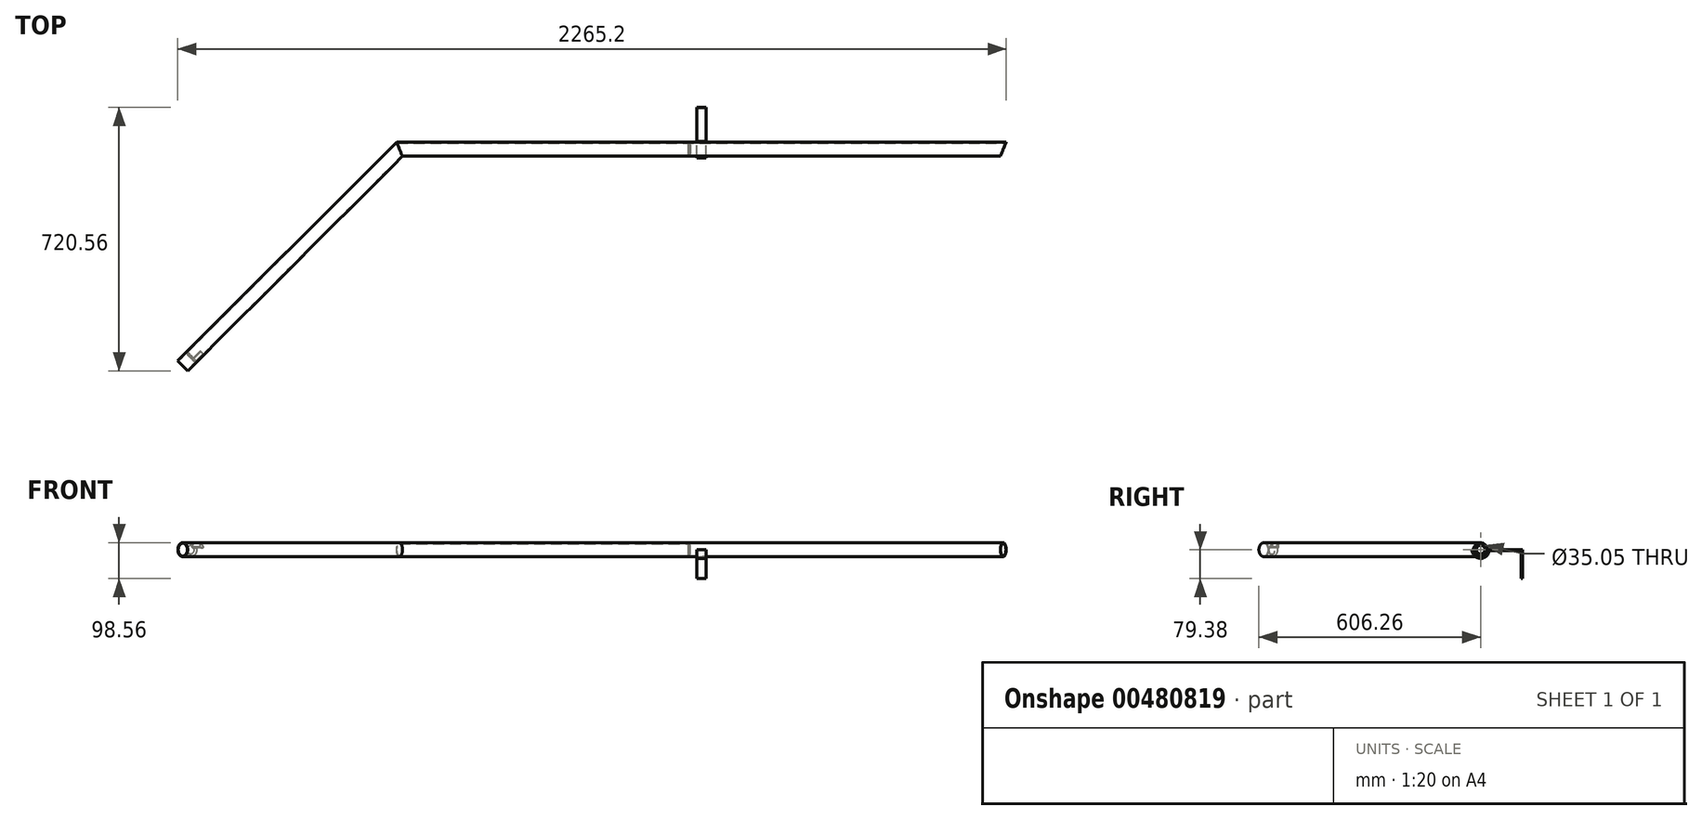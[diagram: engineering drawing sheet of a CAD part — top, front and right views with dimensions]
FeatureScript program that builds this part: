
annotation { "Feature Type Name" : "Feature", "Feature Type Description" : "" }
export const myFeature = defineFeature(function(context is Context, id is Id, definition is map)
    precondition{}
    {
        {
            assignVariable(context, id + "F0", {"name" : "sidelength", "anyValue" : 33});
        }
        {
            assignVariable(context, id + "F1", {"name" : "centerlength", "anyValue" : 65});
        }
        {
            var Q0;
            Q0=qCreatedBy(makeId("Top.planeOp"),FACE);
            var sketch = newSketch(context, id + "F2", { "sketchPlane" : qUnion([Q0])});
            skLineSegment(sketch, "E0", {"start": v(876.3, 114.3) * mm, "end": v(-876.3, 114.3) * mm});
            skLineSegment(sketch, "E1", {"start": v(-876.3, 114.3) * mm, "end": v(-1482.72, -500.56) * mm});
            skLineSegment(sketch, "E2", {"start": v(876.3, 114.3) * mm, "end": v(1482.73, -500.56) * mm});
            skLineSegment(sketch, "E3", {"start": v(-1482.72, -500.56) * mm, "end": v(1482.73, -500.56) * mm});
            skSolve(sketch);
        }
        {
            var Q0;
            Q0=qCreatedBy(makeId("Top.planeOp"),FACE);
            var sketch = newSketch(context, id + "F3", { "sketchPlane" : qUnion([Q0])});
            skLineSegment(sketch, "E4", {"start": v(-1418.2, -592.7) * mm, "end": v(-825.5, 0) * mm});
            skLineSegment(sketch, "E5", {"start": v(-825.5, 0) * mm, "end": v(825.5, 0) * mm});
            skLineSegment(sketch, "E6", {"start": v(825.5, 0) * mm, "end": v(1418.2, -592.7) * mm});
            skLineSegment(sketch, "E7", {"start": v(-825.5, 0) * mm, "end": v(-822.64, -6.9) * mm});
            skSolve(sketch);
        }
        {
            var Q0;
            Q0=sQuery(id+"F3.wireOp",VERTEX,"E4.start");
            var Q1;
            Q1=sQuery(id+"F3.wireOp",EDGE,"E4");
            cPlane(context, id + "F4", {"entities" : qUnion([Q0, Q1]), "cplaneType" : CPlaneType.LINE_POINT, "offset" : 25.4 * mm, "width" : 152.4 * mm, "height" : 152.4 * mm});
        }
        {
            var Q0;
            Q0=sQuery(id+"F3.wireOp",EDGE,"E7");
            cPlane(context, id + "F5", {"entities" : qUnion([Q0]), "cplaneType" : CPlaneType.LINE_ANGLE, "offset" : 25.4 * mm, "angle" : 90 * degree, "width" : 152.4 * mm, "height" : 152.4 * mm});
        }
        {
            var Q0;
            Q0=qCreatedBy(id+"F4.planeOp",FACE);
            var sketch = newSketch(context, id + "F6", { "sketchPlane" : qUnion([Q0])});
            skCircle(sketch, "E8", {"center": v(583.72, 0) * mm, "radius": 19.18 * mm});
            skCircle(sketch, "E9", {"center": v(583.72, 0) * mm, "radius": 17.53 * mm});
            skSolve(sketch);
        }
        {
            var Q0;
            Q0 = qSketchRegion(id + "F6", true);
            var Q1;
            Q1=qCreatedBy(id+"F5.planeOp",FACE);
            extrude(context, id + "F7", {"entities" : qUnion([Q0]), "endBound" : BoundingType.UP_TO_SURFACE, "endBoundEntityFace" : qUnion([Q1]), "depth" : ((getVariable(context, 'sidelength')) + (.1 * getVariable(context, 'sidelength'))) * mm});
        }
        {
            var Q0;
            Q0=qCreatedBy(id+"F4.planeOp",FACE);
            cPlane(context, id + "F8", {"entities" : qUnion([Q0]), "cplaneType" : CPlaneType.OFFSET, "offset" : (getVariable(context, 'sidelength') - 2) * mm, "width" : 152.4 * mm, "height" : 152.4 * mm});
        }
        {
            var Q0;
            Q0=qCreatedBy(id+"F8.planeOp",FACE);
            var sketch = newSketch(context, id + "F9", { "sketchPlane" : qUnion([Q0])});
            skCircle(sketch, "E10", {"center": v(583.72, 0) * mm, "radius": 17.4 * mm});
            skSolve(sketch);
        }
        {
            var Q0;
            Q0 = qSketchRegion(id + "F9", true);
            var Q1;
            Q1=qCreatedBy(id+"F5.planeOp",FACE);
            extrude(context, id + "F10", {"entities" : qUnion([Q0]), "endBound" : BoundingType.UP_TO_SURFACE, "endBoundEntityFace" : qUnion([Q1]), "depth" : 25.4 * mm});
        }
        {
            var Q0;
            Q0=qCreatedBy(makeId("Right.planeOp"),FACE);
            cPlane(context, id + "F11", {"entities" : qUnion([Q0]), "cplaneType" : CPlaneType.OFFSET, "offset" : (getVariable(context, 'centerlength') / 2 - 2) * mm, "oppositeDirection" : true, "width" : 152.4 * mm, "height" : 152.4 * mm});
        }
        {
            var Q0;
            Q0=qCreatedBy(id+"F11.planeOp",FACE);
            var sketch = newSketch(context, id + "F12", { "sketchPlane" : qUnion([Q0])});
            skCircle(sketch, "E11", {"center": v(0, 0) * mm, "radius": 16.9 * mm});
            skSolve(sketch);
        }
        {
            var Q0;
            Q0=makeQuery(id+"F12.imprint","IMPRINT",FACE,{"disambiguationData":[TD([[makeQuery(id+"F12.imprint","IMPRINT",EDGE,{"derivedFrom":sQuery(id+"F12.wireOp",EDGE,"E11")}),1.0]])]});
            var Q1;
            Q1=makeQuery(id+"F10.opExtrude","CAP_FACE",FACE,{"disambiguationData":[OSD([sQuery(id+"F9.wireOp",EDGE,"E10")])],"isStart":false});
            extrude(context, id + "F13", {"entities" : qUnion([Q0]), "operationType" : NewBodyOperationType.ADD, "endBound" : BoundingType.UP_TO_SURFACE, "oppositeDirection" : true, "endBoundEntityFace" : qUnion([Q1]), "depth" : 25.4 * mm});
        }
        {
            var Q0;
            Q0=makeQuery(id+"F10.opExtrude","CAP_FACE",FACE,{"disambiguationData":[OSD([sQuery(id+"F9.wireOp",EDGE,"E10")])],"isStart":true});
            var sketch = newSketch(context, id + "F14", { "sketchPlane" : qUnion([Q0])});
            skCircle(sketch, "E12", {"center": v(-583.72, 0) * mm, "radius": 8.9 * mm, "construction": true});
            skLineSegment(sketch, "E13", {"start": v(-583.72, 0) * mm, "end": v(-583.72, 17.4) * mm, "construction": true});
            skLineSegment(sketch, "E14", {"start": v(-583.72, 0) * mm, "end": v(-566.32, 0) * mm, "construction": true});
            skLineSegment(sketch, "E15", {"start": v(-576.42, 5.08) * mm, "end": v(-567.08, 5.08) * mm});
            skArc(sketch, "E16", {"start": v(-578.64, 7.3) * mm, "mid": v(-577.43, 6.29) * mm, "end": v(-576.42, 5.08) * mm});
            skLineSegment(sketch, "E17", {"start": v(-578.64, 7.3) * mm, "end": v(-578.64, 16.64) * mm});
            skArc(sketch, "E18", {"start": v(-578.64, 16.64) * mm, "mid": v(-571.41, 12.3) * mm, "end": v(-567.08, 5.08) * mm});
            skSolve(sketch);
        }
        {
            var Q0;
            Q0 = qSketchRegion(id + "F14", true);
            extrude(context, id + "F15", {"entities" : qUnion([Q0]), "operationType" : NewBodyOperationType.REMOVE, "oppositeDirection" : true, "depth" : 31.75 * mm, "offsetDistance" : 25.4 * mm});
        }
        {
            var Q0;
            {var subQ0=sQuery(id+"F9.wireOp",EDGE,"E10");var subQ4=makeQuery(id+"F15.boolean.opBoolean","COPY",FACE,{"derivedFrom":makeQuery(id+"F15.opExtrude","SWEPT_FACE",FACE,{"disambiguationData":[OSD([sQuery(id+"F14.wireOp",EDGE,"NrfxDNrx-Ji7I-Meca-oNIs-p1KaCWfqXKCt")])]})});Q0=makeQuery(id+"FA1yCE69HmIhhTY_2.3.F15.boolean.opBoolean","SPLIT",EDGE,{"disambiguationData":[TD([subQ4])],"derivedFrom":makeQuery(id+"FA1yCE69HmIhhTY_2.2.F15.boolean.opBoolean","SPLIT",EDGE,{"disambiguationData":[TD([subQ4])],"derivedFrom":makeQuery(id+"FA1yCE69HmIhhTY_2.1.F15.boolean.opBoolean","SPLIT",EDGE,{"disambiguationData":[TD([subQ4])],"derivedFrom":makeQuery(id+"F10.opExtrude","CAP_EDGE",EDGE,{"disambiguationData":[OSD([subQ0])],"isStart":true})})})});}
            var Q1;
            {var subQ0=sQuery(id+"F9.wireOp",EDGE,"E10");Q1=makeQuery(id+"FA1yCE69HmIhhTY_2.1.F15.boolean.opBoolean","SPLIT",EDGE,{"disambiguationData":[TD([makeQuery(id+"F15.boolean.opBoolean","COPY",FACE,{"derivedFrom":makeQuery(id+"F15.opExtrude","SWEPT_FACE",FACE,{"disambiguationData":[OSD([sQuery(id+"F14.wireOp",EDGE,"E15")])]})})])],"derivedFrom":makeQuery(id+"F10.opExtrude","CAP_EDGE",EDGE,{"disambiguationData":[OSD([subQ0])],"isStart":true})});}
            var Q2;
            {var subQ0=sQuery(id+"F9.wireOp",EDGE,"E10");var subQ3=sQuery(id+"F14.wireOp",EDGE,"NrfxDNrx-Ji7I-Meca-oNIs-p1KaCWfqXKCt");var subQ4=makeQuery(id+"FA1yCE69HmIhhTY_2.1.F15.opExtrude","SWEPT_FACE",FACE,{"disambiguationData":[OSD([sQuery(id+"F14.wireOp",EDGE,"E15")])]});Q2=makeQuery(id+"FA1yCE69HmIhhTY_2.2.F15.boolean.opBoolean","SPLIT",EDGE,{"disambiguationData":[TD([makeQuery(id+"FA1yCE69HmIhhTY_2.1.F15.boolean.opBoolean","COPY",FACE,{"derivedFrom":subQ4})])],"derivedFrom":makeQuery(id+"FA1yCE69HmIhhTY_2.1.F15.boolean.opBoolean","SPLIT",EDGE,{"disambiguationData":[TD([makeQuery(id+"F15.boolean.opBoolean","COPY",FACE,{"derivedFrom":makeQuery(id+"F15.opExtrude","SWEPT_FACE",FACE,{"disambiguationData":[OSD([subQ3])]})})])],"derivedFrom":makeQuery(id+"F10.opExtrude","CAP_EDGE",EDGE,{"disambiguationData":[OSD([subQ0])],"isStart":true})})});}
            var Q3;
            {var subQ0=sQuery(id+"F9.wireOp",EDGE,"E10");var subQ3=sQuery(id+"F14.wireOp",EDGE,"E15");var subQ4=makeQuery(id+"FA1yCE69HmIhhTY_2.2.F15.opExtrude","SWEPT_FACE",FACE,{"disambiguationData":[OSD([subQ3])]});var subQ5=sQuery(id+"F14.wireOp",EDGE,"NrfxDNrx-Ji7I-Meca-oNIs-p1KaCWfqXKCt");var subQ6=makeQuery(id+"F15.boolean.opBoolean","COPY",FACE,{"derivedFrom":makeQuery(id+"F15.opExtrude","SWEPT_FACE",FACE,{"disambiguationData":[OSD([subQ5])]})});Q3=makeQuery(id+"FA1yCE69HmIhhTY_2.3.F15.boolean.opBoolean","SPLIT",EDGE,{"disambiguationData":[TD([makeQuery(id+"FA1yCE69HmIhhTY_2.2.F15.boolean.opBoolean","COPY",FACE,{"derivedFrom":subQ4})])],"derivedFrom":makeQuery(id+"FA1yCE69HmIhhTY_2.2.F15.boolean.opBoolean","SPLIT",EDGE,{"disambiguationData":[TD([subQ6])],"derivedFrom":makeQuery(id+"FA1yCE69HmIhhTY_2.1.F15.boolean.opBoolean","SPLIT",EDGE,{"disambiguationData":[TD([subQ6])],"derivedFrom":makeQuery(id+"F10.opExtrude","CAP_EDGE",EDGE,{"disambiguationData":[OSD([subQ0])],"isStart":true})})})});}
            var Q4;
            Q4=makeQuery(id+"FA1yCE69HmIhhTY_2.1.F15.boolean.opBoolean","COPY",EDGE,{"derivedFrom":makeQuery(id+"FA1yCE69HmIhhTY_2.1.F15.opExtrude","CAP_EDGE",EDGE,{"disambiguationData":[OSD([sQuery(id+"F14.wireOp",EDGE,"IRBFJSMZ-iEYh-WlK5-UFEq-rIrruMqGYSe5")])],"isStart":false})});
            var Q5;
            Q5=makeQuery(id+"F15.boolean.opBoolean","COPY",EDGE,{"derivedFrom":makeQuery(id+"F15.opExtrude","CAP_EDGE",EDGE,{"disambiguationData":[OSD([sQuery(id+"F14.wireOp",EDGE,"IRBFJSMZ-iEYh-WlK5-UFEq-rIrruMqGYSe5")])],"isStart":false})});
            var Q6;
            Q6=makeQuery(id+"FA1yCE69HmIhhTY_2.3.F15.boolean.opBoolean","COPY",EDGE,{"derivedFrom":makeQuery(id+"FA1yCE69HmIhhTY_2.3.F15.opExtrude","CAP_EDGE",EDGE,{"disambiguationData":[OSD([sQuery(id+"F14.wireOp",EDGE,"IRBFJSMZ-iEYh-WlK5-UFEq-rIrruMqGYSe5")])],"isStart":false})});
            var Q7;
            Q7=makeQuery(id+"FA1yCE69HmIhhTY_2.2.F15.boolean.opBoolean","COPY",EDGE,{"derivedFrom":makeQuery(id+"FA1yCE69HmIhhTY_2.2.F15.opExtrude","CAP_EDGE",EDGE,{"disambiguationData":[OSD([sQuery(id+"F14.wireOp",EDGE,"IRBFJSMZ-iEYh-WlK5-UFEq-rIrruMqGYSe5")])],"isStart":false})});
            var Q8;
            {var subQ0=sQuery(id+"F12.wireOp",EDGE,"E11");var subQ2=sQuery(id+"F14.wireOp",EDGE,"NrfxDNrx-Ji7I-Meca-oNIs-p1KaCWfqXKCt");var subQ4=makeQuery(id+"F39BUFb9CijZ2vK_2.1.FA1yCE69HmIhhTY_2.1.F15.opExtrude","SWEPT_FACE",FACE,{"disambiguationData":[OSD([sQuery(id+"F14.wireOp",EDGE,"E15")])]});Q8=makeQuery(id+"F39BUFb9CijZ2vK_2.1.FA1yCE69HmIhhTY_2.2.F15.boolean.opBoolean","SPLIT",EDGE,{"disambiguationData":[TD([makeQuery(id+"F39BUFb9CijZ2vK_2.1.FA1yCE69HmIhhTY_2.1.F15.boolean.opBoolean","COPY",FACE,{"derivedFrom":subQ4})])],"derivedFrom":makeQuery(id+"F39BUFb9CijZ2vK_2.1.FA1yCE69HmIhhTY_2.1.F15.boolean.opBoolean","SPLIT",EDGE,{"disambiguationData":[TD([makeQuery(id+"F39BUFb9CijZ2vK_2.1.F15.boolean.opBoolean","COPY",FACE,{"derivedFrom":makeQuery(id+"F39BUFb9CijZ2vK_2.1.F15.opExtrude","SWEPT_FACE",FACE,{"disambiguationData":[OSD([subQ2])]})})])],"derivedFrom":makeQuery(id+"F13.opExtrude","CAP_EDGE",EDGE,{"disambiguationData":[OSD([subQ0])],"isStart":true})})});}
            var Q9;
            {var subQ0=sQuery(id+"F12.wireOp",EDGE,"E11");var subQ3=sQuery(id+"F14.wireOp",EDGE,"E15");var subQ4=makeQuery(id+"F39BUFb9CijZ2vK_2.1.FA1yCE69HmIhhTY_2.2.F15.opExtrude","SWEPT_FACE",FACE,{"disambiguationData":[OSD([subQ3])]});var subQ5=sQuery(id+"F14.wireOp",EDGE,"NrfxDNrx-Ji7I-Meca-oNIs-p1KaCWfqXKCt");var subQ6=makeQuery(id+"F39BUFb9CijZ2vK_2.1.F15.boolean.opBoolean","COPY",FACE,{"derivedFrom":makeQuery(id+"F39BUFb9CijZ2vK_2.1.F15.opExtrude","SWEPT_FACE",FACE,{"disambiguationData":[OSD([subQ5])]})});Q9=makeQuery(id+"F39BUFb9CijZ2vK_2.1.FA1yCE69HmIhhTY_2.3.F15.boolean.opBoolean","SPLIT",EDGE,{"disambiguationData":[TD([makeQuery(id+"F39BUFb9CijZ2vK_2.1.FA1yCE69HmIhhTY_2.2.F15.boolean.opBoolean","COPY",FACE,{"derivedFrom":subQ4})])],"derivedFrom":makeQuery(id+"F39BUFb9CijZ2vK_2.1.FA1yCE69HmIhhTY_2.2.F15.boolean.opBoolean","SPLIT",EDGE,{"disambiguationData":[TD([subQ6])],"derivedFrom":makeQuery(id+"F39BUFb9CijZ2vK_2.1.FA1yCE69HmIhhTY_2.1.F15.boolean.opBoolean","SPLIT",EDGE,{"disambiguationData":[TD([subQ6])],"derivedFrom":makeQuery(id+"F13.opExtrude","CAP_EDGE",EDGE,{"disambiguationData":[OSD([subQ0])],"isStart":true})})})});}
            var Q10;
            {var subQ0=sQuery(id+"F12.wireOp",EDGE,"E11");var subQ4=makeQuery(id+"F39BUFb9CijZ2vK_2.1.F15.boolean.opBoolean","COPY",FACE,{"derivedFrom":makeQuery(id+"F39BUFb9CijZ2vK_2.1.F15.opExtrude","SWEPT_FACE",FACE,{"disambiguationData":[OSD([sQuery(id+"F14.wireOp",EDGE,"NrfxDNrx-Ji7I-Meca-oNIs-p1KaCWfqXKCt")])]})});Q10=makeQuery(id+"F39BUFb9CijZ2vK_2.1.FA1yCE69HmIhhTY_2.3.F15.boolean.opBoolean","SPLIT",EDGE,{"disambiguationData":[TD([subQ4])],"derivedFrom":makeQuery(id+"F39BUFb9CijZ2vK_2.1.FA1yCE69HmIhhTY_2.2.F15.boolean.opBoolean","SPLIT",EDGE,{"disambiguationData":[TD([subQ4])],"derivedFrom":makeQuery(id+"F39BUFb9CijZ2vK_2.1.FA1yCE69HmIhhTY_2.1.F15.boolean.opBoolean","SPLIT",EDGE,{"disambiguationData":[TD([subQ4])],"derivedFrom":makeQuery(id+"F13.opExtrude","CAP_EDGE",EDGE,{"disambiguationData":[OSD([subQ0])],"isStart":true})})})});}
            var Q11;
            {var subQ0=sQuery(id+"F12.wireOp",EDGE,"E11");Q11=makeQuery(id+"F39BUFb9CijZ2vK_2.1.FA1yCE69HmIhhTY_2.1.F15.boolean.opBoolean","SPLIT",EDGE,{"disambiguationData":[TD([makeQuery(id+"F39BUFb9CijZ2vK_2.1.F15.boolean.opBoolean","COPY",FACE,{"derivedFrom":makeQuery(id+"F39BUFb9CijZ2vK_2.1.F15.opExtrude","SWEPT_FACE",FACE,{"disambiguationData":[OSD([sQuery(id+"F14.wireOp",EDGE,"E15")])]})})])],"derivedFrom":makeQuery(id+"F13.opExtrude","CAP_EDGE",EDGE,{"disambiguationData":[OSD([subQ0])],"isStart":true})});}
            var Q12;
            Q12=makeQuery(id+"F39BUFb9CijZ2vK_2.1.FA1yCE69HmIhhTY_2.1.F15.boolean.opBoolean","INTERSECT",EDGE,{"derivedFrom":[makeQuery(id+"F13.opExtrude","SWEPT_FACE",FACE,{"disambiguationData":[OSD([sQuery(id+"F12.wireOp",EDGE,"E11")])]}),makeQuery(id+"F39BUFb9CijZ2vK_2.1.FA1yCE69HmIhhTY_2.1.F15.opExtrude","CAP_FACE",FACE,{"disambiguationData":[OSD([sQuery(id+"F14.wireOp",EDGE,"E15"),sQuery(id+"F14.wireOp",EDGE,"E16"),sQuery(id+"F14.wireOp",EDGE,"E17"),sQuery(id+"F14.wireOp",EDGE,"E18")])],"isStart":false})]});
            var Q13;
            Q13=makeQuery(id+"F39BUFb9CijZ2vK_2.1.FA1yCE69HmIhhTY_2.2.F15.boolean.opBoolean","INTERSECT",EDGE,{"derivedFrom":[makeQuery(id+"F13.opExtrude","SWEPT_FACE",FACE,{"disambiguationData":[OSD([sQuery(id+"F12.wireOp",EDGE,"E11")])]}),makeQuery(id+"F39BUFb9CijZ2vK_2.1.FA1yCE69HmIhhTY_2.2.F15.opExtrude","CAP_FACE",FACE,{"disambiguationData":[OSD([sQuery(id+"F14.wireOp",EDGE,"E15"),sQuery(id+"F14.wireOp",EDGE,"E16"),sQuery(id+"F14.wireOp",EDGE,"E17"),sQuery(id+"F14.wireOp",EDGE,"E18")])],"isStart":false})]});
            var Q14;
            Q14=makeQuery(id+"F39BUFb9CijZ2vK_2.1.F15.boolean.opBoolean","INTERSECT",EDGE,{"derivedFrom":[makeQuery(id+"F13.opExtrude","SWEPT_FACE",FACE,{"disambiguationData":[OSD([sQuery(id+"F12.wireOp",EDGE,"E11")])]}),makeQuery(id+"F39BUFb9CijZ2vK_2.1.F15.opExtrude","CAP_FACE",FACE,{"disambiguationData":[OSD([sQuery(id+"F14.wireOp",EDGE,"E15"),sQuery(id+"F14.wireOp",EDGE,"E16"),sQuery(id+"F14.wireOp",EDGE,"E17"),sQuery(id+"F14.wireOp",EDGE,"E18")])],"isStart":false})]});
            var Q15;
            Q15=makeQuery(id+"F39BUFb9CijZ2vK_2.1.FA1yCE69HmIhhTY_2.3.F15.boolean.opBoolean","INTERSECT",EDGE,{"derivedFrom":[makeQuery(id+"F13.opExtrude","SWEPT_FACE",FACE,{"disambiguationData":[OSD([sQuery(id+"F12.wireOp",EDGE,"E11")])]}),makeQuery(id+"F39BUFb9CijZ2vK_2.1.FA1yCE69HmIhhTY_2.3.F15.opExtrude","CAP_FACE",FACE,{"disambiguationData":[OSD([sQuery(id+"F14.wireOp",EDGE,"E15"),sQuery(id+"F14.wireOp",EDGE,"E16"),sQuery(id+"F14.wireOp",EDGE,"E17"),sQuery(id+"F14.wireOp",EDGE,"E18")])],"isStart":false})]});
            var Q16;
            {var subQ0=sQuery(id+"F9.wireOp",EDGE,"E10");var subQ3=makeQuery(id+"F15.boolean.opBoolean","COPY",FACE,{"derivedFrom":makeQuery(id+"F15.opExtrude","SWEPT_FACE",FACE,{"disambiguationData":[OSD([sQuery(id+"F14.wireOp",EDGE,"E17")])]})});Q16=makeQuery(id+"FA1yCE69HmIhhTY_2.3.F15.boolean.opBoolean","SPLIT",EDGE,{"disambiguationData":[TD([subQ3])],"derivedFrom":makeQuery(id+"FA1yCE69HmIhhTY_2.2.F15.boolean.opBoolean","SPLIT",EDGE,{"disambiguationData":[TD([subQ3])],"derivedFrom":makeQuery(id+"FA1yCE69HmIhhTY_2.1.F15.boolean.opBoolean","SPLIT",EDGE,{"disambiguationData":[TD([subQ3])],"derivedFrom":makeQuery(id+"F10.opExtrude","CAP_EDGE",EDGE,{"disambiguationData":[OSD([subQ0])],"isStart":true})})})});}
            var Q17;
            {var subQ0=sQuery(id+"F9.wireOp",EDGE,"E10");var subQ3=sQuery(id+"F14.wireOp",EDGE,"E15");var subQ4=makeQuery(id+"FA1yCE69HmIhhTY_2.2.F15.opExtrude","SWEPT_FACE",FACE,{"disambiguationData":[OSD([subQ3])]});var subQ5=sQuery(id+"F14.wireOp",EDGE,"E17");var subQ6=makeQuery(id+"F15.boolean.opBoolean","COPY",FACE,{"derivedFrom":makeQuery(id+"F15.opExtrude","SWEPT_FACE",FACE,{"disambiguationData":[OSD([subQ5])]})});Q17=makeQuery(id+"FA1yCE69HmIhhTY_2.3.F15.boolean.opBoolean","SPLIT",EDGE,{"disambiguationData":[TD([makeQuery(id+"FA1yCE69HmIhhTY_2.2.F15.boolean.opBoolean","COPY",FACE,{"derivedFrom":subQ4})])],"derivedFrom":makeQuery(id+"FA1yCE69HmIhhTY_2.2.F15.boolean.opBoolean","SPLIT",EDGE,{"disambiguationData":[TD([subQ6])],"derivedFrom":makeQuery(id+"FA1yCE69HmIhhTY_2.1.F15.boolean.opBoolean","SPLIT",EDGE,{"disambiguationData":[TD([subQ6])],"derivedFrom":makeQuery(id+"F10.opExtrude","CAP_EDGE",EDGE,{"disambiguationData":[OSD([subQ0])],"isStart":true})})})});}
            var Q18;
            {var subQ0=sQuery(id+"F9.wireOp",EDGE,"E10");var subQ3=makeQuery(id+"FA1yCE69HmIhhTY_2.1.F15.opExtrude","SWEPT_FACE",FACE,{"disambiguationData":[OSD([sQuery(id+"F14.wireOp",EDGE,"E15")])]});var subQ4=sQuery(id+"F14.wireOp",EDGE,"E17");Q18=makeQuery(id+"FA1yCE69HmIhhTY_2.2.F15.boolean.opBoolean","SPLIT",EDGE,{"disambiguationData":[TD([makeQuery(id+"FA1yCE69HmIhhTY_2.1.F15.boolean.opBoolean","COPY",FACE,{"derivedFrom":subQ3})])],"derivedFrom":makeQuery(id+"FA1yCE69HmIhhTY_2.1.F15.boolean.opBoolean","SPLIT",EDGE,{"disambiguationData":[TD([makeQuery(id+"F15.boolean.opBoolean","COPY",FACE,{"derivedFrom":makeQuery(id+"F15.opExtrude","SWEPT_FACE",FACE,{"disambiguationData":[OSD([subQ4])]})})])],"derivedFrom":makeQuery(id+"F10.opExtrude","CAP_EDGE",EDGE,{"disambiguationData":[OSD([subQ0])],"isStart":true})})});}
            var Q19;
            {var subQ0=sQuery(id+"F12.wireOp",EDGE,"E11");var subQ3=makeQuery(id+"F39BUFb9CijZ2vK_2.1.F15.boolean.opBoolean","COPY",FACE,{"derivedFrom":makeQuery(id+"F39BUFb9CijZ2vK_2.1.F15.opExtrude","SWEPT_FACE",FACE,{"disambiguationData":[OSD([sQuery(id+"F14.wireOp",EDGE,"E17")])]})});Q19=makeQuery(id+"F39BUFb9CijZ2vK_2.1.FA1yCE69HmIhhTY_2.3.F15.boolean.opBoolean","SPLIT",EDGE,{"disambiguationData":[TD([subQ3])],"derivedFrom":makeQuery(id+"F39BUFb9CijZ2vK_2.1.FA1yCE69HmIhhTY_2.2.F15.boolean.opBoolean","SPLIT",EDGE,{"disambiguationData":[TD([subQ3])],"derivedFrom":makeQuery(id+"F39BUFb9CijZ2vK_2.1.FA1yCE69HmIhhTY_2.1.F15.boolean.opBoolean","SPLIT",EDGE,{"disambiguationData":[TD([subQ3])],"derivedFrom":makeQuery(id+"F13.opExtrude","CAP_EDGE",EDGE,{"disambiguationData":[OSD([subQ0])],"isStart":true})})})});}
            var Q20;
            {var subQ0=sQuery(id+"F12.wireOp",EDGE,"E11");var subQ2=makeQuery(id+"F39BUFb9CijZ2vK_2.1.FA1yCE69HmIhhTY_2.1.F15.opExtrude","SWEPT_FACE",FACE,{"disambiguationData":[OSD([sQuery(id+"F14.wireOp",EDGE,"E15")])]});var subQ3=sQuery(id+"F14.wireOp",EDGE,"E17");Q20=makeQuery(id+"F39BUFb9CijZ2vK_2.1.FA1yCE69HmIhhTY_2.2.F15.boolean.opBoolean","SPLIT",EDGE,{"disambiguationData":[TD([makeQuery(id+"F39BUFb9CijZ2vK_2.1.FA1yCE69HmIhhTY_2.1.F15.boolean.opBoolean","COPY",FACE,{"derivedFrom":subQ2})])],"derivedFrom":makeQuery(id+"F39BUFb9CijZ2vK_2.1.FA1yCE69HmIhhTY_2.1.F15.boolean.opBoolean","SPLIT",EDGE,{"disambiguationData":[TD([makeQuery(id+"F39BUFb9CijZ2vK_2.1.F15.boolean.opBoolean","COPY",FACE,{"derivedFrom":makeQuery(id+"F39BUFb9CijZ2vK_2.1.F15.opExtrude","SWEPT_FACE",FACE,{"disambiguationData":[OSD([subQ3])]})})])],"derivedFrom":makeQuery(id+"F13.opExtrude","CAP_EDGE",EDGE,{"disambiguationData":[OSD([subQ0])],"isStart":true})})});}
            var Q21;
            {var subQ0=sQuery(id+"F12.wireOp",EDGE,"E11");var subQ3=sQuery(id+"F14.wireOp",EDGE,"E15");var subQ4=makeQuery(id+"F39BUFb9CijZ2vK_2.1.FA1yCE69HmIhhTY_2.2.F15.opExtrude","SWEPT_FACE",FACE,{"disambiguationData":[OSD([subQ3])]});var subQ5=sQuery(id+"F14.wireOp",EDGE,"E17");var subQ6=makeQuery(id+"F39BUFb9CijZ2vK_2.1.F15.boolean.opBoolean","COPY",FACE,{"derivedFrom":makeQuery(id+"F39BUFb9CijZ2vK_2.1.F15.opExtrude","SWEPT_FACE",FACE,{"disambiguationData":[OSD([subQ5])]})});Q21=makeQuery(id+"F39BUFb9CijZ2vK_2.1.FA1yCE69HmIhhTY_2.3.F15.boolean.opBoolean","SPLIT",EDGE,{"disambiguationData":[TD([makeQuery(id+"F39BUFb9CijZ2vK_2.1.FA1yCE69HmIhhTY_2.2.F15.boolean.opBoolean","COPY",FACE,{"derivedFrom":subQ4})])],"derivedFrom":makeQuery(id+"F39BUFb9CijZ2vK_2.1.FA1yCE69HmIhhTY_2.2.F15.boolean.opBoolean","SPLIT",EDGE,{"disambiguationData":[TD([subQ6])],"derivedFrom":makeQuery(id+"F39BUFb9CijZ2vK_2.1.FA1yCE69HmIhhTY_2.1.F15.boolean.opBoolean","SPLIT",EDGE,{"disambiguationData":[TD([subQ6])],"derivedFrom":makeQuery(id+"F13.opExtrude","CAP_EDGE",EDGE,{"disambiguationData":[OSD([subQ0])],"isStart":true})})})});}
            chamfer(context, id + "F16", {"entities" : qUnion([Q0, Q1, Q2, Q3, Q4, Q5, Q6, Q7, Q8, Q9, Q10, Q11, Q12, Q13, Q14, Q15, Q16, Q17, Q18, Q19, Q20, Q21]), "width" : 5.08 * mm, "tangentPropagation" : true});
        }
        {
            var Q0;
            Q0=qCreatedBy(makeId("Right.planeOp"),FACE);
            var sketch = newSketch(context, id + "F17", { "sketchPlane" : qUnion([Q0])});
            skCircle(sketch, "E19", {"center": v(0, 0) * mm, "radius": 19.18 * mm});
            skCircle(sketch, "E20", {"center": v(0, 0) * mm, "radius": 17.53 * mm});
            skSolve(sketch);
        }
        {
            var Q0;
            Q0 = qSketchRegion(id + "F17", true);
            var Q1;
            Q1=qCreatedBy(id+"F5.planeOp",FACE);
            extrude(context, id + "F18", {"entities" : qUnion([Q0]), "endBound" : BoundingType.UP_TO_SURFACE, "oppositeDirection" : true, "depth" : 25.4 * mm, "endBoundEntityFace" : qUnion([Q1]), "offsetDistance" : 25.4 * mm});
        }
        {
            var Q0;
            Q0=makeQuery(id+"F18.opExtrude","SWEPT_BODY",BODY,{"disambiguationData":[OSD([sQuery(id+"F17.wireOp",EDGE,"E19"),sQuery(id+"F17.wireOp",EDGE,"E20")])]});
            var Q1;
            Q1=qCreatedBy(makeId("Right.planeOp"),FACE);
            mirror(context, id + "F19", {"operationType" : NewBodyOperationType.ADD, "entities" : qUnion([Q0]), "mirrorPlane" : qUnion([Q1])});
        }
        {
            var Q0;
            Q0=qCreatedBy(makeId("Right.planeOp"),FACE);
            var sketch = newSketch(context, id + "F20", { "sketchPlane" : qUnion([Q0])});
            skCircle(sketch, "E21", {"center": v(0, 0) * mm, "radius": 20.64 * mm, "construction": true});
            skCircle(sketch, "E22", {"center": v(0, 0) * mm, "radius": 23.81 * mm, "construction": true});
            skLineSegment(sketch, "E23", {"start": v(23.81, 0) * mm, "end": v(114.3, 0) * mm});
            skLineSegment(sketch, "E24", {"start": v(114.3, 0) * mm, "end": v(114.3, -79.38) * mm});
            skLineSegment(sketch, "E25", {"start": v(114.3, -79.38) * mm, "end": v(111.13, -79.38) * mm});
            skLineSegment(sketch, "E26", {"start": v(111.13, -79.38) * mm, "end": v(111.13, -3.17) * mm});
            skLineSegment(sketch, "E27", {"start": v(111.13, -3.17) * mm, "end": v(23.6, -3.18) * mm});
            skArc(sketch, "E28", {"start": v(20.64, 0) * mm, "mid": v(0, -20.64) * mm, "end": v(-20.64, 0) * mm});
            skArc(sketch, "E29", {"start": v(-23.81, 0) * mm, "mid": v(-1.6, -23.76) * mm, "end": v(23.6, -3.18) * mm});
            skLineSegment(sketch, "E30", {"start": v(-23.81, 0) * mm, "end": v(-20.64, 0) * mm});
            skLineSegment(sketch, "E31", {"start": v(20.64, 0) * mm, "end": v(23.81, 0) * mm});
            skSolve(sketch);
        }
        {
            var Q0;
            Q0 = qSketchRegion(id + "F20", true);
            extrude(context, id + "F21", {"entities" : qUnion([Q0]), "endBound" : BoundingType.SYMMETRIC, "depth" : 25.4 * mm, "offsetDistance" : 25.4 * mm});
        }
    });
